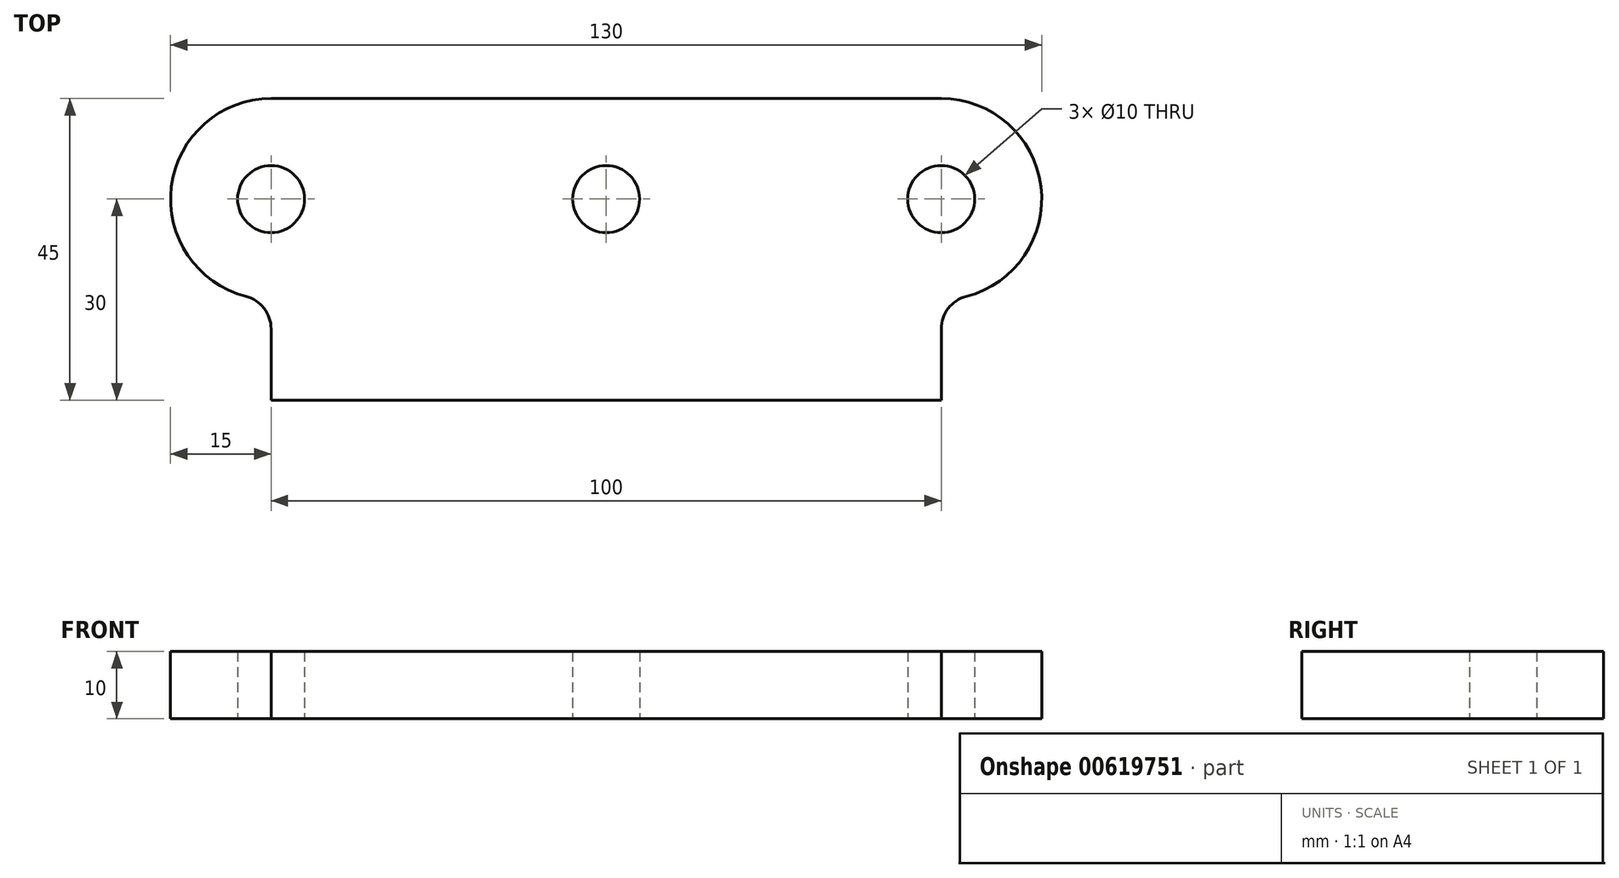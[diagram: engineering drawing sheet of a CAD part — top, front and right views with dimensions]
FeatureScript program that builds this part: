
annotation { "Feature Type Name" : "Feature", "Feature Type Description" : "" }
export const myFeature = defineFeature(function(context is Context, id is Id, definition is map)
    precondition{}
    {
        {
            var Q0;
            Q0=qCreatedBy(makeId("Top.planeOp"),FACE);
            var sketch = newSketch(context, id + "F0", { "sketchPlane" : qUnion([Q0])});
            skLineSegment(sketch, "E0", {"start": v(0, 0) * mm, "end": v(0, 19.77) * mm, "construction": true});
            skLineSegment(sketch, "E1", {"start": v(0, 0) * mm, "end": v(0, -30) * mm, "construction": true});
            skLineSegment(sketch, "E2.bottom", {"start": v(-50, 15) * mm, "end": v(0, 15) * mm});
            skLineSegment(sketch, "E2.top", {"start": v(-50, -30) * mm, "end": v(0, -30) * mm});
            skLineSegment(sketch, "E2.right", {"start": v(0, 15) * mm, "end": v(0, -30) * mm});
            skLineSegment(sketch, "E3", {"start": v(0, 0) * mm, "end": v(-50, 0) * mm, "construction": true});
            skLineSegment(sketch, "E4", {"start": v(0, 0) * mm, "end": v(50, 0) * mm});
            skCircle(sketch, "E5", {"center": v(-50, 0) * mm, "radius": 5 * mm});
            skArc(sketch, "E6", {"start": v(-50, 15) * mm, "mid": v(-64.88, 1.9) * mm, "end": v(-53.75, -14.52) * mm});
            skLineSegment(sketch, "E7.trimOffspring", {"start": v(-50, -19.36) * mm, "end": v(-50, -30) * mm});
            skArc(sketch, "E8.filletArc", {"start": v(-50, -19.36) * mm, "mid": v(-51.05, -16.3) * mm, "end": v(-53.75, -14.52) * mm});
            skCircle(sketch, "E9", {"center": v(0, 0) * mm, "radius": 5 * mm});
            skLineSegment(sketch, "E10.MirrorCS", {"start": v(50, 15) * mm, "end": v(0, 15) * mm});
            skArc(sketch, "E11.MirrorCS", {"start": v(50, 15) * mm, "mid": v(64.88, 1.9) * mm, "end": v(53.75, -14.52) * mm});
            skArc(sketch, "E12.MirrorCS", {"start": v(50, -19.36) * mm, "mid": v(51.05, -16.3) * mm, "end": v(53.75, -14.52) * mm});
            skLineSegment(sketch, "E13.MirrorCS", {"start": v(50, -19.36) * mm, "end": v(50, -30) * mm});
            skLineSegment(sketch, "E14.MirrorCS", {"start": v(50, -30) * mm, "end": v(0, -30) * mm});
            skCircle(sketch, "E15.MirrorC", {"center": v(50, 0) * mm, "radius": 5 * mm});
            skSolve(sketch);
        }
        {
            var Q0;
            {var subQ1=sQuery(id+"F0.wireOp",EDGE,"E2.bottom");Q0=makeQuery(id+"F0.imprint","IMPRINT",FACE,{"disambiguationData":[TD([[makeQuery(id+"F0.imprint","IMPRINT",EDGE,{"derivedFrom":subQ1}),-1.0]])]});}
            var Q1;
            {var subQ4=sQuery(id+"F0.wireOp",EDGE,"E10.MirrorCS");Q1=makeQuery(id+"F0.imprint","IMPRINT",FACE,{"disambiguationData":[TD([[makeQuery(id+"F0.imprint","IMPRINT",EDGE,{"derivedFrom":subQ4}),1.0]])]});}
            extrude(context, id + "F1", {"entities" : qUnion([Q0, Q1]), "depth" : 10 * mm, "offsetDistance" : 25 * mm});
        }
    });
